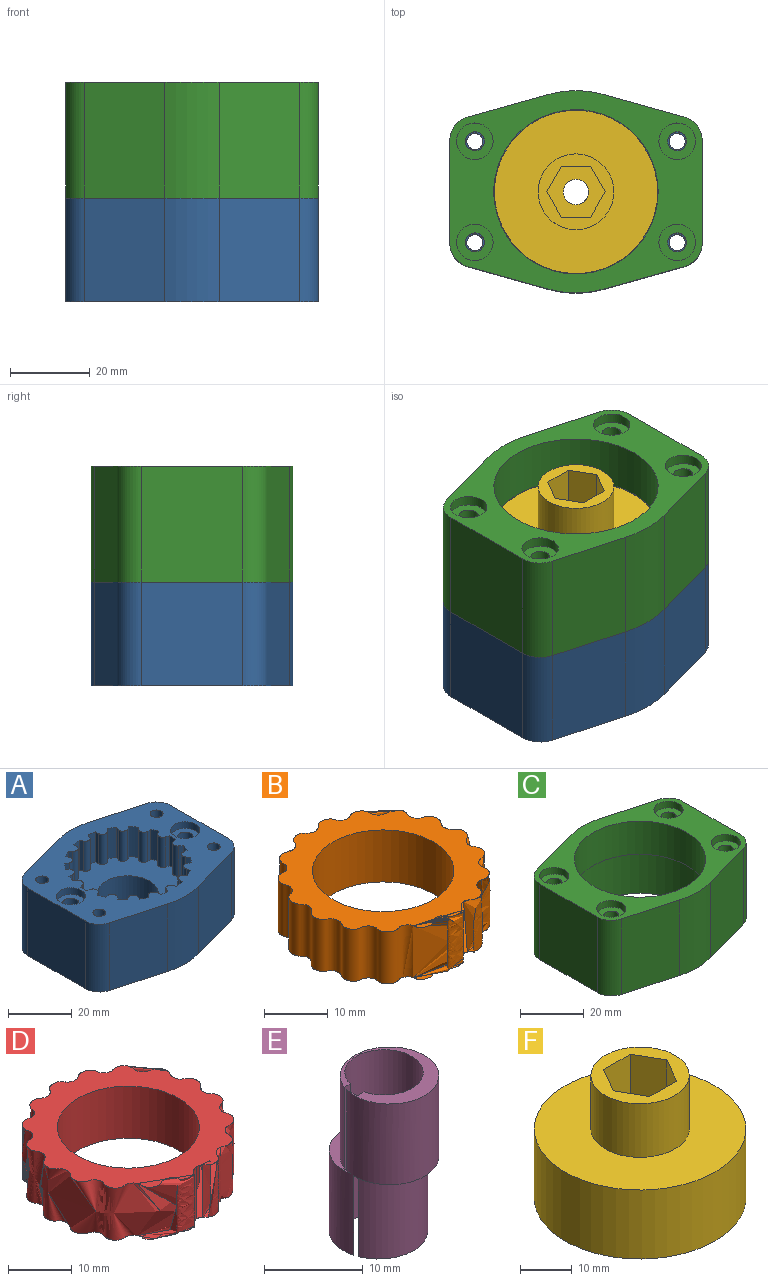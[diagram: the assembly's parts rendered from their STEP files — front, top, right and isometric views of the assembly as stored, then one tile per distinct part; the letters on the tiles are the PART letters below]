
ASSEMBLY  parts=6 mates=10
PART A: 98 faces, bbox 63.5x50.8x26 mm
  f0: cylinder r=2.55mm len=23.43mm, axis (0,0,-1), area 375.9mm2, adj f19,f97
  f1: cylinder r=2.55mm len=23.43mm, axis (0,0,-1), area 375.9mm2, adj f19,f95
  f2: plane 63.5x50.8mm, normal (0,0,1), area 1463.5mm2, adj f3,f4,f5,f6,f7,f8,f9,f10
  f3: plane 26x25.4mm, normal (1,0,0), area 660.4mm2, adj f2,f4,f17,f19
  f4: cylinder r=6.35mm len=26mm, axis (0,0,-1), area 214.5mm2, adj f2,f3,f5,f19
  f5: plane 26x20.29mm, normal (0.27,0.96,0), area 547.6mm2, adj f2,f4,f6,f19
  f6: cylinder r=25.4mm len=26mm, axis (0,0,-1), area 358.8mm2, adj f2,f5,f7,f19
  f7: plane 26x20.29mm, normal (-0.27,0.96,0), area 547.6mm2, adj f2,f6,f8,f19
  f8: cylinder r=6.35mm len=26mm, axis (0,0,-1), area 214.5mm2, adj f2,f7,f9,f19
  f9: plane 26x25.4mm, normal (-1,0,0), area 660.4mm2, adj f2,f8,f10,f19
  f10: cylinder r=6.35mm len=26mm, axis (0,0,-1), area 214.5mm2, adj f2,f9,f11,f19
  f11: plane 26x20.29mm, normal (-0.27,-0.96,0), area 547.6mm2, adj f2,f10,f12,f19
  f12: cylinder r=25.4mm len=26mm, axis (0,0,-1), area 358.8mm2, adj f2,f11,f13,f19
  f13: plane 26x20.29mm, normal (0.27,-0.96,0), area 547.6mm2, adj f2,f12,f17,f19
  f14: cylinder r=2.02mm len=26mm, axis (0,0,-1), area 329.9mm2, adj f2,f19
  f15: cylinder r=2.02mm len=26mm, axis (0,0,-1), area 329.9mm2, adj f2,f19
  f16: cylinder r=2.02mm len=26mm, axis (0,0,-1), area 329.9mm2, adj f2,f19
  f17: cylinder r=6.35mm len=26mm, axis (0,0,-1), area 214.5mm2, adj f2,f3,f13,f19
  f18: cylinder r=2.02mm len=26mm, axis (0,0,-1), area 329.9mm2, adj f2,f19
  f19: plane 63.5x50.8mm, normal (0,0,-1), area 2383.2mm2, adj f0,f1,f3,f4,f5,f6,f7,f8
  f20: cylinder r=19.84mm len=11.57mm, axis (0,0,1), area 33.7mm2, adj f2,f21,f91,f92
  f21: plane 11.57x1.04mm, normal (-0.74,0.68,0), area 16.3mm2, adj f2,f20,f22,f92
  f22: cylinder r=1.59mm len=11.57mm, axis (0,0,1), area 43.3mm2, adj f2,f21,f23,f92
  f23: plane 11.57x1.41mm, normal (1,0.04,0), area 16.3mm2, adj f2,f22,f24,f92
  f24: cylinder r=19.84mm len=11.57mm, axis (0,0,1), area 33.7mm2, adj f2,f23,f25,f92
  f25: plane 11.57x1.3mm, normal (-0.92,0.38,0), area 16.3mm2, adj f2,f24,f26,f92
  f26: cylinder r=1.59mm len=11.57mm, axis (0,0,1), area 43.3mm2, adj f2,f25,f27,f92
  f27: plane 11.57x1.3mm, normal (0.92,0.38,0), area 16.3mm2, adj f2,f26,f28,f92
  f28: cylinder r=19.84mm len=11.57mm, axis (0,0,1), area 33.7mm2, adj f2,f27,f29,f92
  f29: plane 11.57x1.41mm, normal (-1,0.04,0), area 16.3mm2, adj f2,f28,f30,f92
  f30: cylinder r=1.59mm len=11.57mm, axis (0,0,1), area 43.3mm2, adj f2,f29,f31,f92
  f31: plane 11.57x1.04mm, normal (0.74,0.68,0), area 16.3mm2, adj f2,f30,f32,f92
  f32: cylinder r=19.84mm len=11.57mm, axis (0,0,1), area 33.7mm2, adj f2,f31,f33,f92
  f33: plane 11.57x1.34mm, normal (-0.95,-0.3,0), area 16.3mm2, adj f2,f32,f34,f92
  f34: cylinder r=1.59mm len=11.57mm, axis (0,0,1), area 43.3mm2, adj f2,f33,f35,f92
  f35: plane 11.57x1.25mm, normal (0.46,0.89,0), area 16.3mm2, adj f2,f34,f36,f92
  f36: cylinder r=19.84mm len=11.57mm, axis (0,0,1), area 33.7mm2, adj f2,f35,f37,f92
  f37: plane 11.57x1.12mm, normal (-0.79,-0.61,0), area 16.3mm2, adj f2,f36,f38,f92
  f38: cylinder r=1.59mm len=11.57mm, axis (0,0,1), area 43.3mm2, adj f2,f37,f39,f92
  f39: plane 11.57x1.39mm, normal (0.13,0.99,0), area 16.3mm2, adj f2,f38,f40,f92
  f40: cylinder r=19.84mm len=11.57mm, axis (0,0,1), area 33.7mm2, adj f2,f39,f41,f92
  f41: plane 11.57x1.19mm, normal (-0.54,-0.84,0), area 16.3mm2, adj f2,f40,f42,f92
  f42: cylinder r=1.59mm len=11.57mm, axis (0,0,1), area 43.3mm2, adj f2,f41,f43,f92
  f43: plane 11.57x1.37mm, normal (-0.22,0.98,0), area 16.3mm2, adj f2,f42,f44,f92
  f44: cylinder r=19.84mm len=11.57mm, axis (0,0,1), area 33.7mm2, adj f2,f43,f45,f92
  f45: plane 11.57x1.37mm, normal (-0.22,-0.98,0), area 16.3mm2, adj f2,f44,f46,f92
  f46: cylinder r=1.59mm len=11.57mm, axis (0,0,1), area 43.3mm2, adj f2,f45,f47,f92
  f47: plane 11.57x1.19mm, normal (-0.54,0.84,0), area 16.3mm2, adj f2,f46,f48,f92
  f48: cylinder r=19.84mm len=11.57mm, axis (0,0,1), area 33.7mm2, adj f2,f47,f49,f92
  f49: plane 11.57x1.39mm, normal (0.13,-0.99,0), area 16.3mm2, adj f2,f48,f50,f92
  f50: cylinder r=1.59mm len=11.57mm, axis (0,0,1), area 43.3mm2, adj f2,f49,f51,f92
  f51: plane 11.57x1.12mm, normal (-0.79,0.61,0), area 16.3mm2, adj f2,f50,f52,f92
  f52: cylinder r=19.84mm len=11.57mm, axis (0,0,1), area 33.7mm2, adj f2,f51,f53,f92
  f53: plane 11.57x1.25mm, normal (0.46,-0.89,0), area 16.3mm2, adj f2,f52,f54,f92
  f54: cylinder r=1.59mm len=11.57mm, axis (0,0,1), area 43.3mm2, adj f2,f53,f55,f92
  f55: plane 11.57x1.34mm, normal (-0.95,0.3,0), area 16.3mm2, adj f2,f54,f56,f92
  f56: cylinder r=19.84mm len=11.57mm, axis (0,0,1), area 33.7mm2, adj f2,f55,f57,f92
  f57: plane 11.57x1.04mm, normal (0.74,-0.68,0), area 16.3mm2, adj f2,f56,f58,f92
  f58: cylinder r=1.59mm len=11.57mm, axis (0,0,1), area 43.3mm2, adj f2,f57,f59,f92
  f59: plane 11.57x1.41mm, normal (-1,-0.04,0), area 16.3mm2, adj f2,f58,f60,f92
  f60: cylinder r=19.84mm len=11.57mm, axis (0,0,1), area 33.7mm2, adj f2,f59,f61,f92
  f61: plane 11.57x1.3mm, normal (0.92,-0.38,0), area 16.3mm2, adj f2,f60,f62,f92
  f62: cylinder r=1.59mm len=11.57mm, axis (0,0,1), area 43.3mm2, adj f2,f61,f63,f92
  f63: plane 11.57x1.3mm, normal (-0.92,-0.38,0), area 16.3mm2, adj f2,f62,f64,f92
  f64: cylinder r=19.84mm len=11.57mm, axis (0,0,1), area 33.7mm2, adj f2,f63,f65,f92
  f65: plane 11.57x1.41mm, normal (1,-0.04,0), area 16.3mm2, adj f2,f64,f66,f92
  f66: cylinder r=1.59mm len=11.57mm, axis (0,0,1), area 43.3mm2, adj f2,f65,f67,f92
  f67: plane 11.57x1.04mm, normal (-0.74,-0.68,0), area 16.3mm2, adj f2,f66,f68,f92
  f68: cylinder r=19.84mm len=11.57mm, axis (0,0,1), area 33.7mm2, adj f2,f67,f69,f92
  f69: plane 11.57x1.34mm, normal (0.95,0.3,0), area 16.3mm2, adj f2,f68,f70,f92
  f70: cylinder r=1.59mm len=11.57mm, axis (0,0,1), area 43.3mm2, adj f2,f69,f71,f92
  f71: plane 11.57x1.25mm, normal (-0.46,-0.89,0), area 16.3mm2, adj f2,f70,f72,f92
  f72: cylinder r=19.84mm len=11.57mm, axis (0,0,1), area 33.7mm2, adj f2,f71,f73,f92
  f73: plane 11.57x1.12mm, normal (0.79,0.61,0), area 16.3mm2, adj f2,f72,f74,f92
  f74: cylinder r=1.59mm len=11.57mm, axis (0,0,1), area 43.3mm2, adj f2,f73,f75,f92
  f75: plane 11.57x1.39mm, normal (-0.13,-0.99,0), area 16.3mm2, adj f2,f74,f76,f92
  f76: cylinder r=19.84mm len=11.57mm, axis (0,0,1), area 33.7mm2, adj f2,f75,f77,f92
  f77: plane 11.57x1.19mm, normal (0.54,0.84,0), area 16.3mm2, adj f2,f76,f78,f92
  f78: cylinder r=1.59mm len=11.57mm, axis (0,0,1), area 43.3mm2, adj f2,f77,f79,f92
  f79: plane 11.57x1.37mm, normal (0.22,-0.98,0), area 16.3mm2, adj f2,f78,f80,f92
  f80: cylinder r=19.84mm len=11.57mm, axis (0,0,1), area 33.7mm2, adj f2,f79,f81,f92
  f81: plane 11.57x1.37mm, normal (0.22,0.98,0), area 16.3mm2, adj f2,f80,f82,f92
  f82: cylinder r=1.59mm len=11.57mm, axis (0,0,1), area 43.3mm2, adj f2,f81,f83,f92
  f83: plane 11.57x1.19mm, normal (0.54,-0.84,0), area 16.3mm2, adj f2,f82,f84,f92
  f84: cylinder r=19.84mm len=11.57mm, axis (0,0,1), area 33.7mm2, adj f2,f83,f85,f92
  f85: plane 11.57x1.39mm, normal (-0.13,0.99,0), area 16.3mm2, adj f2,f84,f86,f92
  f86: cylinder r=1.59mm len=11.57mm, axis (0,0,1), area 43.3mm2, adj f2,f85,f87,f92
  f87: plane 11.57x1.12mm, normal (0.79,-0.61,0), area 16.3mm2, adj f2,f86,f88,f92
  f88: cylinder r=19.84mm len=11.57mm, axis (0,0,1), area 33.7mm2, adj f2,f87,f89,f92
  f89: plane 11.57x1.25mm, normal (-0.46,0.89,0), area 16.3mm2, adj f2,f88,f90,f92
  f90: cylinder r=1.59mm len=11.57mm, axis (0,0,1), area 43.3mm2, adj f2,f89,f91,f92
  f91: plane 11.57x1.34mm, normal (0.95,-0.3,0), area 16.3mm2, adj f2,f20,f90,f92
  f92: plane 39.69x39.48mm, normal (0,0,1), area 828.5mm2, adj f20,f21,f22,f23,f24,f25,f26,f27
  f93: cylinder r=9.53mm len=19.05mm, axis (0,0,1), area 863.3mm2, adj f19,f92
  f94: cylinder r=4.58mm len=9.17mm, axis (0,0,1), area 73.9mm2, adj f2,f95
  f95: plane 9.17x9.17mm, normal (0,0,1), area 45.6mm2, adj f1,f94
  f96: cylinder r=4.58mm len=9.17mm, axis (0,0,1), area 73.9mm2, adj f2,f97
  f97: plane 9.17x9.17mm, normal (0,0,1), area 45.6mm2, adj f0,f96
PART B: 4 faces, bbox 94.1x94.1x70.9 mm
  f0: extruded ~33.17x31.96mm, area 0mm2, adj f1,f3
  f1: plane 94.11x93.99mm, normal (0,0,1), area 424.5mm2, adj f0,f2
  f2: cylinder r=11.11mm len=22.23mm, axis (0,0,-1), area 698.2mm2, adj f1,f3
  f3: plane 94.11x93.99mm, normal (0,0,-1), area 424.5mm2, adj f0,f2
PART C: 29 faces, bbox 63.5x50.8x29.1 mm
  f0: cylinder r=2.38mm len=26.48mm, axis (0,0,-1), area 396.3mm2, adj f17,f26
  f1: cylinder r=2.38mm len=26.48mm, axis (0,0,-1), area 396.3mm2, adj f17,f24
  f2: cylinder r=2.38mm len=26.48mm, axis (0,0,-1), area 396.3mm2, adj f17,f22
  f3: cylinder r=2.38mm len=26.48mm, axis (0,0,-1), area 396.3mm2, adj f17,f28
  f4: plane 29.05x25.4mm, normal (1,0,0), area 737.9mm2, adj f5,f15,f16,f17
  f5: cylinder r=6.35mm len=29.05mm, axis (0,0,-1), area 239.6mm2, adj f4,f6,f16,f17
  f6: plane 29.05x20.29mm, normal (0.27,0.96,0), area 611.8mm2, adj f5,f7,f16,f17
  f7: cylinder r=25.4mm len=29.05mm, axis (0,0,-1), area 400.9mm2, adj f6,f8,f16,f17
  f8: plane 29.05x20.29mm, normal (-0.27,0.96,0), area 611.8mm2, adj f7,f9,f16,f17
  f9: cylinder r=6.35mm len=29.05mm, axis (0,0,-1), area 239.6mm2, adj f8,f10,f16,f17
  f10: plane 29.05x25.4mm, normal (-1,0,0), area 737.9mm2, adj f9,f11,f16,f17
  f11: cylinder r=6.35mm len=29.05mm, axis (0,0,-1), area 239.6mm2, adj f10,f12,f16,f17
  f12: plane 29.05x20.29mm, normal (-0.27,-0.96,0), area 611.8mm2, adj f11,f13,f16,f17
  f13: cylinder r=25.4mm len=29.05mm, axis (0,0,-1), area 400.9mm2, adj f12,f14,f16,f17
  f14: plane 29.05x20.29mm, normal (0.27,-0.96,0), area 611.8mm2, adj f13,f15,f16,f17
  f15: cylinder r=6.35mm len=29.05mm, axis (0,0,-1), area 239.6mm2, adj f4,f14,f16,f17
  f16: plane 63.5x50.8mm, normal (0,0,1), area 1158.2mm2, adj f4,f5,f6,f7,f8,f9,f10,f11
  f17: plane 63.5x50.8mm, normal (0,0,-1), area 1098.7mm2, adj f0,f1,f2,f3,f4,f5,f6,f7
  f18: cylinder r=22.5mm len=45mm, axis (0,0,-1), area 2311.4mm2, adj f17,f19
  f19: plane 45x45mm, normal (0,0,-1), area 252.4mm2, adj f18,f20
  f20: cylinder r=20.64mm len=41.28mm, axis (0,0,1), area 1646.8mm2, adj f16,f19
  f21: cylinder r=4.58mm len=9.17mm, axis (0,0,1), area 73.9mm2, adj f16,f22
  f22: plane 9.17x9.17mm, normal (0,0,1), area 48.2mm2, adj f2,f21
  f23: cylinder r=4.58mm len=9.17mm, axis (0,0,1), area 73.9mm2, adj f16,f24
  f24: plane 9.17x9.17mm, normal (0,0,1), area 48.2mm2, adj f1,f23
  f25: cylinder r=4.58mm len=9.17mm, axis (0,0,1), area 73.9mm2, adj f16,f26
  f26: plane 9.17x9.17mm, normal (0,0,1), area 48.2mm2, adj f0,f25
  f27: cylinder r=4.58mm len=9.17mm, axis (0,0,1), area 73.9mm2, adj f16,f28
  f28: plane 9.17x9.17mm, normal (0,0,1), area 48.2mm2, adj f3,f27
PART D: 4 faces, bbox 94.1x94.1x70.9 mm
  f0: extruded ~33.07x31.41mm, area 0mm2, adj f1,f3
  f1: plane 94.11x93.99mm, normal (0,0,1), area 424.5mm2, adj f0,f2
  f2: cylinder r=11.11mm len=22.23mm, axis (0,0,-1), area 698.2mm2, adj f1,f3
  f3: plane 94.11x93.99mm, normal (0,0,-1), area 424.5mm2, adj f0,f2
PART E: 10 faces, bbox 10x11.6x20 mm
  f0: cylinder r=5mm len=10mm, axis (0,0,-1), area 308.9mm2, adj f1,f2,f3,f7,f8
  f1: plane 10x5.79mm, normal (0,0,1), area 15.8mm2, adj f0,f4,f7,f9
  f2: plane 10x10mm, normal (0,0,-1), area 27.3mm2, adj f0,f6,f7,f8,f9
  f3: plane 10x5.79mm, normal (0,0,-1), area 15.8mm2, adj f0,f4,f7,f8
  f4: cylinder r=5mm len=10mm, axis (0,0,-1), area 308.9mm2, adj f1,f3,f5,f7,f9
  f5: plane 10x10mm, normal (0,0,1), area 27.3mm2, adj f4,f6,f7,f8,f9
  f6: cylinder r=3.97mm len=20mm, axis (0,0,-1), area 458.3mm2, adj f2,f5,f8,f9
  f7: plane 20x2mm, normal (1,0,0), area 29.9mm2, adj f0,f1,f2,f3,f4,f5,f8,f9
  f8: plane 20x0.99mm, normal (0,1,0), area 18.2mm2, adj f0,f2,f3,f5,f6,f7
  f9: plane 20x0.99mm, normal (0,-1,0), area 18.2mm2, adj f1,f2,f4,f5,f6,f7
PART F: 88 faces, bbox 41x41x29.1 mm
  f0: plane 41x41mm, normal (0,0,1), area 1035.2mm2, adj f1,f81
  f1: cylinder r=20.5mm len=41mm, axis (0,0,-1), area 2106mm2, adj f0,f2
  f2: plane 41x41mm, normal (0,0,-1), area 360.8mm2, adj f1,f3,f4,f5,f6,f7,f8,f9
  f3: cylinder r=1.59mm len=10mm, axis (0,0,-1), area 37.4mm2, adj f2,f4,f74,f75
  f4: plane 10x2.2mm, normal (-0.13,-0.99,0), area 22.2mm2, adj f2,f3,f5,f75
  f5: cylinder r=19.09mm len=10mm, axis (0,0,-1), area 20.2mm2, adj f2,f4,f6,f75
  f6: plane 10x1.88mm, normal (0.54,0.84,0), area 22.2mm2, adj f2,f5,f7,f75
  f7: cylinder r=1.59mm len=10mm, axis (0,0,-1), area 37.4mm2, adj f2,f6,f8,f75
  f8: plane 10x2.17mm, normal (0.22,-0.98,0), area 22.2mm2, adj f2,f7,f9,f75
  f9: cylinder r=19.09mm len=10mm, axis (0,0,-1), area 20.2mm2, adj f2,f8,f10,f75
  f10: plane 10x2.17mm, normal (0.22,0.98,0), area 22.2mm2, adj f2,f9,f11,f75
  f11: cylinder r=1.59mm len=10mm, axis (0,0,-1), area 37.4mm2, adj f2,f10,f12,f75
  f12: plane 10x1.88mm, normal (0.54,-0.84,0), area 22.2mm2, adj f2,f11,f13,f75
  f13: cylinder r=19.09mm len=10mm, axis (0,0,-1), area 20.2mm2, adj f2,f12,f14,f75
  f14: plane 10x2.2mm, normal (-0.13,0.99,0), area 22.2mm2, adj f2,f13,f15,f75
  f15: cylinder r=1.59mm len=10mm, axis (0,0,-1), area 37.4mm2, adj f2,f14,f16,f75
  f16: plane 10x1.76mm, normal (0.79,-0.61,0), area 22.2mm2, adj f2,f15,f17,f75
  f17: cylinder r=19.09mm len=10mm, axis (0,0,-1), area 20.2mm2, adj f2,f16,f18,f75
  f18: plane 10x1.97mm, normal (-0.46,0.89,0), area 22.2mm2, adj f2,f17,f19,f75
  f19: cylinder r=1.59mm len=10mm, axis (0,0,-1), area 37.4mm2, adj f2,f18,f20,f75
  f20: plane 10x2.12mm, normal (0.95,-0.3,0), area 22.2mm2, adj f2,f19,f21,f75
  f21: cylinder r=19.09mm len=10mm, axis (0,0,-1), area 20.2mm2, adj f2,f20,f22,f75
  f22: plane 10x1.64mm, normal (-0.74,0.68,0), area 22.2mm2, adj f2,f21,f23,f75
  f23: cylinder r=1.59mm len=10mm, axis (0,0,-1), area 37.4mm2, adj f2,f22,f24,f75
  f24: plane 10x2.22mm, normal (1,0.04,0), area 22.2mm2, adj f2,f23,f25,f75
  f25: cylinder r=19.09mm len=10mm, axis (0,0,-1), area 20.2mm2, adj f2,f24,f26,f75
  f26: plane 10x2.05mm, normal (-0.92,0.38,0), area 22.2mm2, adj f2,f25,f27,f75
  f27: cylinder r=1.59mm len=10mm, axis (0,0,-1), area 37.4mm2, adj f2,f26,f28,f75
  f28: plane 10x2.05mm, normal (0.92,0.38,0), area 22.2mm2, adj f2,f27,f29,f75
  f29: cylinder r=19.09mm len=10mm, axis (0,0,-1), area 20.2mm2, adj f2,f28,f30,f75
  f30: plane 10x2.22mm, normal (-1,0.04,0), area 22.2mm2, adj f2,f29,f31,f75
  f31: cylinder r=1.59mm len=10mm, axis (0,0,-1), area 37.4mm2, adj f2,f30,f32,f75
  f32: plane 10x1.64mm, normal (0.74,0.68,0), area 22.2mm2, adj f2,f31,f33,f75
  f33: cylinder r=19.09mm len=10mm, axis (0,0,-1), area 20.2mm2, adj f2,f32,f34,f75
  f34: plane 10x2.12mm, normal (-0.95,-0.3,0), area 22.2mm2, adj f2,f33,f35,f75
  f35: cylinder r=1.59mm len=10mm, axis (0,0,-1), area 37.4mm2, adj f2,f34,f36,f75
  f36: plane 10x1.97mm, normal (0.46,0.89,0), area 22.2mm2, adj f2,f35,f37,f75
  f37: cylinder r=19.09mm len=10mm, axis (0,0,-1), area 20.2mm2, adj f2,f36,f38,f75
  f38: plane 10x1.76mm, normal (-0.79,-0.61,0), area 22.2mm2, adj f2,f37,f39,f75
  f39: cylinder r=1.59mm len=10mm, axis (0,0,-1), area 37.4mm2, adj f2,f38,f40,f75
  f40: plane 10x2.2mm, normal (0.13,0.99,0), area 22.2mm2, adj f2,f39,f41,f75
  f41: cylinder r=19.09mm len=10mm, axis (0,0,-1), area 20.2mm2, adj f2,f40,f42,f75
  f42: plane 10x1.88mm, normal (-0.54,-0.84,0), area 22.2mm2, adj f2,f41,f43,f75
  f43: cylinder r=1.59mm len=10mm, axis (0,0,-1), area 37.4mm2, adj f2,f42,f44,f75
  f44: plane 10x2.17mm, normal (-0.22,0.98,0), area 22.2mm2, adj f2,f43,f45,f75
  f45: cylinder r=19.09mm len=10mm, axis (0,0,-1), area 20.2mm2, adj f2,f44,f46,f75
  f46: plane 10x2.17mm, normal (-0.22,-0.98,0), area 22.2mm2, adj f2,f45,f47,f75
  f47: cylinder r=1.59mm len=10mm, axis (0,0,-1), area 37.4mm2, adj f2,f46,f48,f75
  f48: plane 10x1.88mm, normal (-0.54,0.84,0), area 22.2mm2, adj f2,f47,f49,f75
  f49: cylinder r=19.09mm len=10mm, axis (0,0,-1), area 20.2mm2, adj f2,f48,f50,f75
  f50: plane 10x2.2mm, normal (0.13,-0.99,0), area 22.2mm2, adj f2,f49,f51,f75
  f51: cylinder r=1.59mm len=10mm, axis (0,0,-1), area 37.4mm2, adj f2,f50,f52,f75
  f52: plane 10x1.76mm, normal (-0.79,0.61,0), area 22.2mm2, adj f2,f51,f53,f75
  f53: cylinder r=19.09mm len=10mm, axis (0,0,-1), area 20.2mm2, adj f2,f52,f54,f75
  f54: plane 10x1.97mm, normal (0.46,-0.89,0), area 22.2mm2, adj f2,f53,f55,f75
  f55: cylinder r=1.59mm len=10mm, axis (0,0,-1), area 37.4mm2, adj f2,f54,f56,f75
  f56: plane 10x2.12mm, normal (-0.95,0.3,0), area 22.2mm2, adj f2,f55,f57,f75
  f57: cylinder r=19.09mm len=10mm, axis (0,0,-1), area 20.2mm2, adj f2,f56,f58,f75
  f58: plane 10x1.64mm, normal (0.74,-0.68,0), area 22.2mm2, adj f2,f57,f59,f75
  f59: cylinder r=1.59mm len=10mm, axis (0,0,-1), area 37.4mm2, adj f2,f58,f60,f75
  f60: plane 10x2.22mm, normal (-1,-0.04,0), area 22.2mm2, adj f2,f59,f61,f75
  f61: cylinder r=19.09mm len=10mm, axis (0,0,-1), area 20.2mm2, adj f2,f60,f62,f75
  f62: plane 10x2.05mm, normal (0.92,-0.38,0), area 22.2mm2, adj f2,f61,f63,f75
  f63: cylinder r=1.59mm len=10mm, axis (0,0,-1), area 37.4mm2, adj f2,f62,f64,f75
  f64: plane 10x2.05mm, normal (-0.92,-0.38,0), area 22.2mm2, adj f2,f63,f65,f75
  f65: cylinder r=19.09mm len=10mm, axis (0,0,-1), area 20.2mm2, adj f2,f64,f66,f75
  f66: plane 10x2.22mm, normal (1,-0.04,0), area 22.2mm2, adj f2,f65,f67,f75
  f67: cylinder r=1.59mm len=10mm, axis (0,0,-1), area 37.4mm2, adj f2,f66,f68,f75
  f68: plane 10x1.64mm, normal (-0.74,-0.68,0), area 22.2mm2, adj f2,f67,f69,f75
  f69: cylinder r=19.09mm len=10mm, axis (0,0,-1), area 20.2mm2, adj f2,f68,f70,f75
  f70: plane 10x2.12mm, normal (0.95,0.3,0), area 22.2mm2, adj f2,f69,f71,f75
  f71: cylinder r=1.59mm len=10mm, axis (0,0,-1), area 37.4mm2, adj f2,f70,f72,f75
  f72: plane 10x1.97mm, normal (-0.46,-0.89,0), area 22.2mm2, adj f2,f71,f73,f75
  f73: cylinder r=19.09mm len=10mm, axis (0,0,-1), area 20.2mm2, adj f2,f72,f74,f75
  f74: plane 10x1.76mm, normal (0.79,0.61,0), area 22.2mm2, adj f2,f3,f73,f75
  f75: plane 38.18x37.89mm, normal (0,0,-1), area 862.7mm2, adj f3,f4,f5,f6,f7,f8,f9,f10
  f76: plane 12.7x6.35mm, normal (0.87,-0.5,0), area 93.1mm2, adj f77,f82,f83,f84
  f77: plane 12.7x7.33mm, normal (0,-1,0), area 93.1mm2, adj f76,f78,f83,f84
  f78: plane 12.7x6.35mm, normal (-0.87,-0.5,0), area 93.1mm2, adj f77,f79,f83,f84
  f79: plane 12.7x6.35mm, normal (-0.87,0.5,0), area 93.1mm2, adj f78,f80,f83,f84
  f80: plane 12.7x7.33mm, normal (0,1,0), area 93.1mm2, adj f79,f82,f83,f84
  f81: cylinder r=9.53mm len=19.05mm, axis (0,0,-1), area 760.1mm2, adj f0,f83
  f82: plane 12.7x6.35mm, normal (0.87,0.5,0), area 93.1mm2, adj f76,f80,f83,f84
  f83: plane 19.05x19.05mm, normal (0,0,1), area 145.3mm2, adj f76,f77,f78,f79,f80,f81,f82
  f84: plane 14.66x12.7mm, normal (0,0,1), area 108mm2, adj f76,f77,f78,f79,f80,f82,f87
  f85: cylinder r=5.55mm len=11.1mm, axis (0,0,-1), area 116.9mm2, adj f75,f86
  f86: plane 11.1x11.1mm, normal (0,0,-1), area 65.1mm2, adj f85,f87
  f87: cylinder r=3.17mm len=6.35mm, axis (0,0,-1), area 59.8mm2, adj f84,f86
PLACE A t=(1.28,15.59,30.1)mm
PLACE B t=(1.28,15.3,44.52)mm
PLACE C t=(1.28,15.59,56.1)mm
PLACE D t=(1.28,15.63,44.52)mm
PLACE E t=(1.28,15.59,44.52)mm
PLACE F t=(1.28,15.59,56.1)mm
MATE cylindrical F.f85 <-> E.f6  axis (0,0,-1) through (1.28,15.59,67.77)mm
MATE cylindrical E.f4 <-> B.f2  axis (0,0,-1) through (1.28,14.8,54.52)mm
MATE cylindrical E.f6 <-> A.f93  axis (0,0,-1) through (1.28,15.59,54.52)mm
MATE planar D.f2 <-> A.f56  axis (0,0,-1) through (1.28,16.38,44.52)mm
MATE cylindrical E.f0 <-> D.f2  axis (0,0,-1) through (1.28,16.38,49.52)mm
MATE planar E.f5 <-> B.f2  axis (0,0,1) through (1.56,13.31,64.52)mm
MATE planar F.f85 <-> A.f20  axis (0,0,-1) through (1.28,15.59,56.1)mm
MATE cylindrical F.f1 <-> C.f18  axis (0,0,-1) through (1.28,15.59,64.27)mm
MATE planar C.f17 <-> A.f20  axis (0,0,-1) through (-30.47,15.59,56.1)mm
MATE planar E.f2 <-> D.f2  axis (0,0,-1) through (1.56,17.87,44.52)mm
